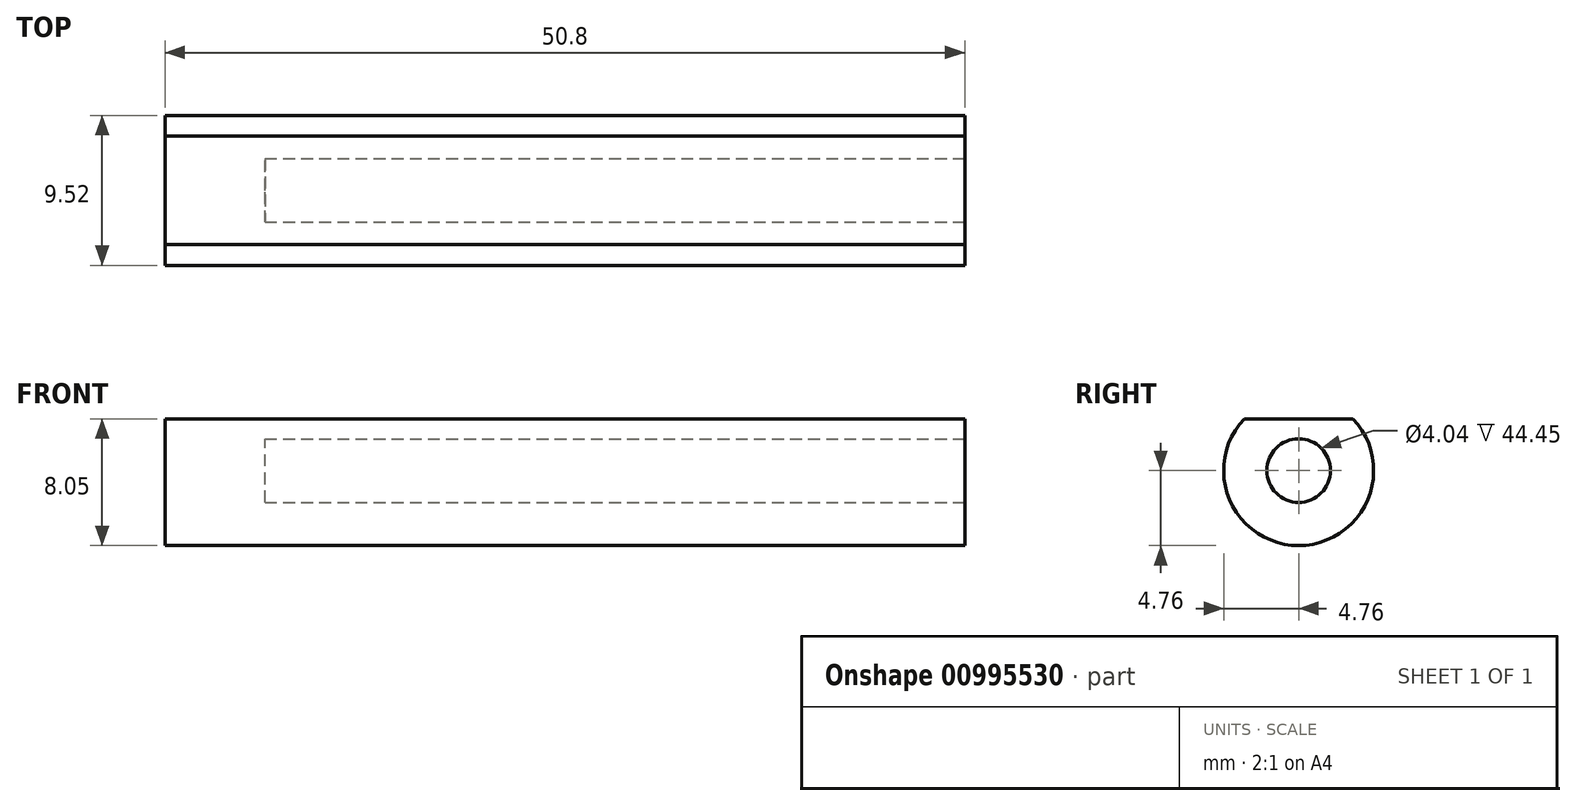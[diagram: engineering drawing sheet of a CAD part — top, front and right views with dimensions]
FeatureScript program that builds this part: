
annotation { "Feature Type Name" : "Feature", "Feature Type Description" : "" }
export const myFeature = defineFeature(function(context is Context, id is Id, definition is map)
    precondition{}
    {
        {
            var Q0;
            Q0=qCreatedBy(makeId("Right.planeOp"),FACE);
            var sketch = newSketch(context, id + "F0", { "sketchPlane" : qUnion([Q0])});
            skCircle(sketch, "E0", {"center": v(0, 0) * mm, "radius": 4.76 * mm});
            skSolve(sketch);
        }
        {
            var Q0;
            Q0=makeQuery(id+"F0.imprint","IMPRINT",FACE,{"disambiguationData":[TD([[makeQuery(id+"F0.imprint","IMPRINT",EDGE,{"derivedFrom":sQuery(id+"F0.wireOp",EDGE,"E0")}),1.0]])]});
            extrude(context, id + "F1", {"entities" : qUnion([Q0]), "depth" : 50.8 * mm, "offsetDistance" : 25.4 * mm});
        }
        {
            var Q0;
            Q0=makeQuery(id+"F1.opExtrude","CAP_FACE",FACE,{"disambiguationData":[OSD([sQuery(id+"F0.wireOp",EDGE,"E0")])],"isStart":false});
            var sketch = newSketch(context, id + "F2", { "sketchPlane" : qUnion([Q0])});
            skArc(sketch, "E1.0.0", {"start": v(3.44, 3.29) * mm, "mid": v(0, 4.76) * mm, "end": v(-3.44, 3.29) * mm});
            skLineSegment(sketch, "E2", {"start": v(-3.44, 3.29) * mm, "end": v(3.44, 3.29) * mm});
            skCircle(sketch, "E3", {"center": v(0, 0) * mm, "radius": 2.02 * mm, "construction": true});
            skSolve(sketch);
        }
        {
            var Q0;
            Q0 = qSketchRegion(id + "F2", true);
            extrude(context, id + "F3", {"entities" : qUnion([Q0]), "operationType" : NewBodyOperationType.REMOVE, "endBound" : BoundingType.THROUGH_ALL, "oppositeDirection" : true, "depth" : 25.4 * mm, "offsetDistance" : 25.4 * mm});
        }
        {
            var Q0;
            Q0=makeQuery(id+"F1.opExtrude","CAP_FACE",FACE,{"disambiguationData":[OSD([sQuery(id+"F0.wireOp",EDGE,"E0")])],"isStart":false});
            var sketch = newSketch(context, id + "F4", { "sketchPlane" : qUnion([Q0])});
            skCircle(sketch, "E4", {"center": v(0, 0) * mm, "radius": 2.02 * mm});
            skSolve(sketch);
        }
        {
            var Q0;
            Q0 = qSketchRegion(id + "F4", true);
            extrude(context, id + "F5", {"entities" : qUnion([Q0]), "operationType" : NewBodyOperationType.REMOVE, "oppositeDirection" : true, "depth" : 44.45 * mm, "offsetDistance" : 25.4 * mm});
        }
    });
